# Revit family: Electrical Actuator-JCI_Sapphire_Plus-(70 bar)Novec1230
name_source: partatom
category: Specialty Equipment
revit_build: Autodesk Revit 2017 (Build: 20171027_0315(x64)
units: mm (PartAtom-declared; Revit-internal decimal feet)

## family parameters
Always vertical = Yes
Cut with Voids When Loaded = No
OmniClass Number = 23.29.33.13.11
Part Type = Normal
Room Calculation Point = No
Round Connector Dimension = Use Diameter
Shared = Yes
Work Plane-Based = Yes

## types (1)
- Actuator Electrical
    Assembly Code = D4090300
    Date Modified = YYYY/MM/DD
    Default Elevation = 1219.2 mm  [stored 4 ft]
    Description = Electrical Actuator Bridge Rectifier
    Equipment Abbreviation = EA
    Equipment Number = XXX
    Family Version = 1.0
    Fire Suppression Agent = 3M™ Novec™ 1230 Fire Protection Fluid
    Height = 0 mm  [stored 0 ft]
    Manufacturer = Johnson Controls, Inc.
    Model = 304700001
    Model Disclaimer = For More Information Contact JOHNSON CONTROLS
    Operating Temperature = 122 °F
    Part Description = Electrical Actuator Bridge Rectifier
    Part Number = 304700001
    Product Documentation Link = http://www.sapphireplus.com
    Product Material = JCI-Metal-Brass-Satin; JCI-Metal-Nickel_Plating
    Product Page URL = http://www.sapphireplus.com
    URL = http://www.sapphireplus.com
    Weight = 0.00 lbf
    Width = 0 mm  [stored 0 ft]

note: [stored X ft] marks values corroborated as IEEE doubles in the binary element streams (Revit-internal decimal feet)

## geometry (parser evidence)
native form markers: Sweep x2
no freeform markers — native parametric forms only
